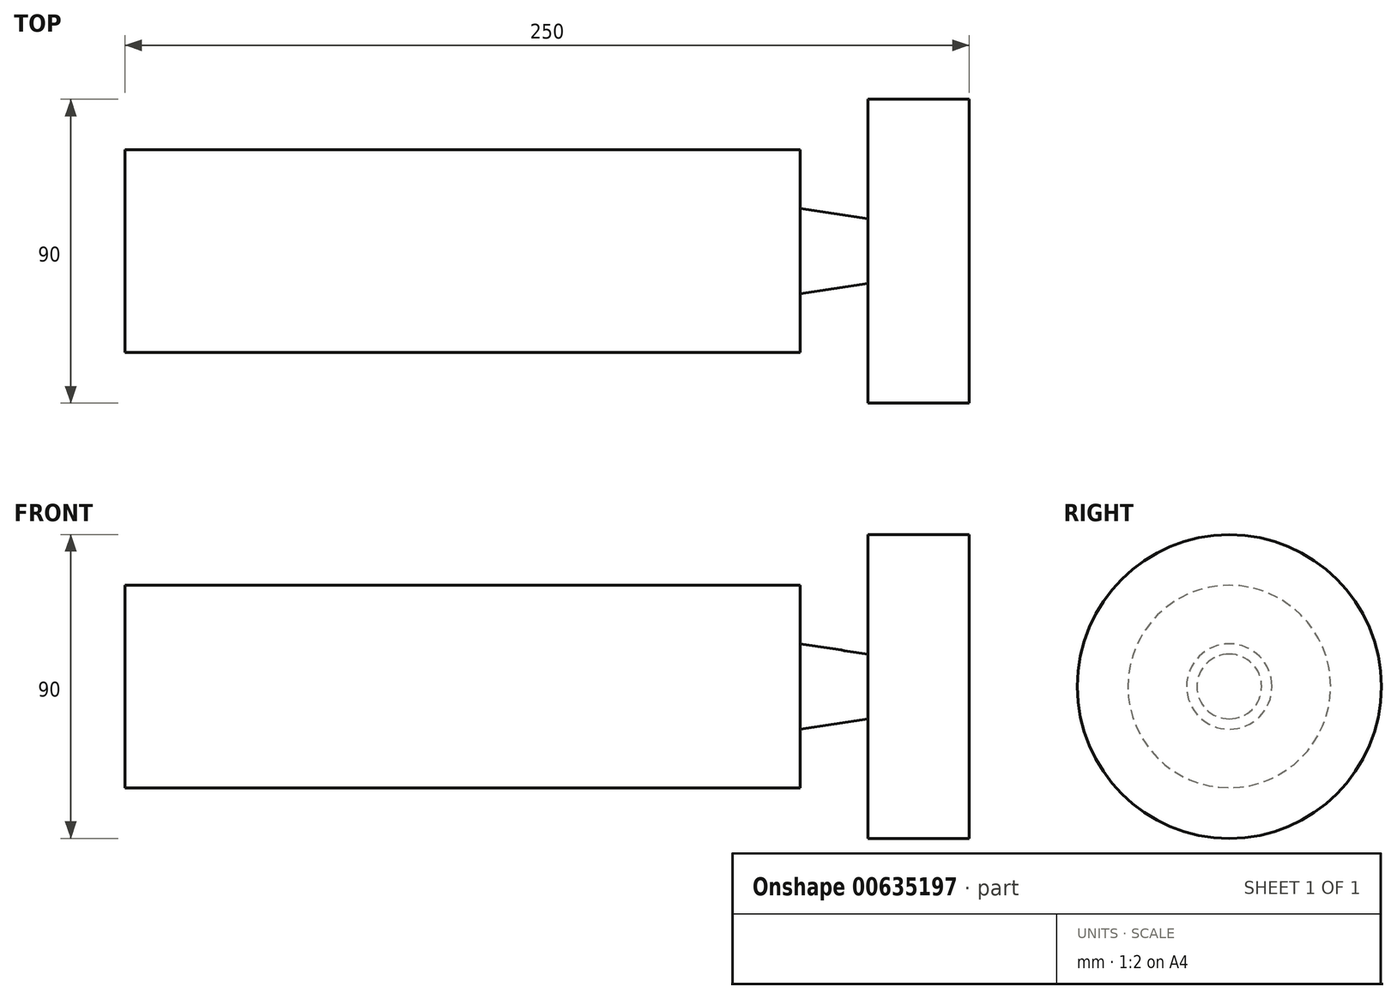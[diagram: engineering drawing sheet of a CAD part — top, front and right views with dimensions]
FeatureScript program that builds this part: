
annotation { "Feature Type Name" : "Feature", "Feature Type Description" : "" }
export const myFeature = defineFeature(function(context is Context, id is Id, definition is map)
    precondition{}
    {
        {
            var Q0;
            Q0=qCreatedBy(makeId("Right.planeOp"),FACE);
            var sketch = newSketch(context, id + "F0", { "sketchPlane" : qUnion([Q0])});
            skCircle(sketch, "E0", {"center": v(0, 0) * mm, "radius": 30 * mm});
            skSolve(sketch);
        }
        {
            var Q0;
            Q0=makeQuery(id+"F0.imprint","IMPRINT",FACE,{"disambiguationData":[TD([[makeQuery(id+"F0.imprint","IMPRINT",EDGE,{"derivedFrom":sQuery(id+"F0.wireOp",EDGE,"E0")}),1.0]])]});
            extrude(context, id + "F1", {"entities" : qUnion([Q0]), "oppositeDirection" : true, "depth" : 200 * mm, "offsetDistance" : 25 * mm});
        }
        {
            var Q0;
            Q0=qCreatedBy(makeId("Top.planeOp"),FACE);
            var sketch = newSketch(context, id + "F2", { "sketchPlane" : qUnion([Q0])});
            skLineSegment(sketch, "E1", {"start": v(0, 0) * mm, "end": v(30.4, 0) * mm});
            skLineSegment(sketch, "E2", {"start": v(30.4, 0) * mm, "end": v(30.4, 8) * mm});
            skLineSegment(sketch, "E3", {"start": v(30.4, 8) * mm, "end": v(0, 12.65) * mm});
            skLineSegment(sketch, "E4", {"start": v(0, 12.65) * mm, "end": v(0, 0) * mm});
            skSolve(sketch);
        }
        {
            var Q0;
            Q0 = qSketchRegion(id + "F2", true);
            var Q1;
            Q1=sQuery(id+"F2.wireOp",EDGE,"E1");
            revolve(context, id + "F3", {"operationType" : NewBodyOperationType.ADD, "entities" : qUnion([Q0]), "axis" : qUnion([Q1]), "revolveType" : RevolveType.FULL});
        }
        {
            var Q0;
            Q0=qCreatedBy(makeId("Right.planeOp"),FACE);
            var sketch = newSketch(context, id + "F4", { "sketchPlane" : qUnion([Q0])});
            skCircle(sketch, "E5", {"center": v(0, 0) * mm, "radius": 45 * mm});
            skSolve(sketch);
        }
        {
            var Q0;
            Q0 = qSketchRegion(id + "F4", true);
            extrude(context, id + "F5", {"entities" : qUnion([Q0]), "operationType" : NewBodyOperationType.ADD, "depth" : 50 * mm, "offsetDistance" : 25 * mm, "hasSecondDirection" : true, "secondDirectionOppositeDirection" : true, "secondDirectionDepth" : -20 * mm});
        }
    });
